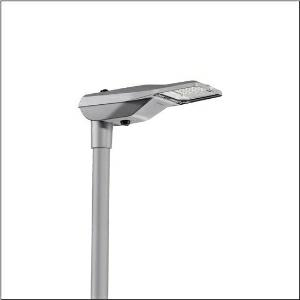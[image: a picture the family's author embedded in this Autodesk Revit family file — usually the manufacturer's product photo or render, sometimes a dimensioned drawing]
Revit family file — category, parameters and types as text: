
# Revit family: streetlight_sl_21_micro___st1_0a_5xe1d43t08db_894b
name_source: partatom
category: Lighting Fixtures
units: mm (PartAtom-declared; Revit-internal decimal feet)

## family parameters
Cut with Voids When Loaded = No
Host = Face
Light Source = No
Part Type = Normal
Room Calculation Point = No
Round Connector Dimension = Use Diameter
Shared = No

## types (1)
- --- (1 x LED, 5320 lm, 39.1 W, 4000K)
    Apparent Load = 39 VA
    CIE Flux Codes = 37 72 97 100 100
    Color Rendering = 70
    Color Temperature = 4000K
    Default Elevation = 1800 mm
    Description = Streetlight SL 21 micro, mast luminaire, primary light control with lens, of PMMA, primary optical cover: cover, of toughened safety glass, transparent, light distribution: ST1.0a, light emission: direct distribution, primary light characteristic: asymmetric, installation type: side-entry, post-top, LED, High Power LED, rated luminous flux: 5.320lm, luminous efficacy: 136lm/W, light colour: 740, colour temperature: 4000K, control gear: D4i, control: flexible luminous flux parameterisation, time-dependent luminous flux control, constant luminous flux control, overheat protection, pre-setting: logarithmic dimming characteristic, mains connection: 220..240V, AC, 50/60Hz, start of lifetime: 39W, end of service life: 41W, reduction: 18W, luminaire housing, of diecast aluminium, powder-coated, SITECO metallic grey (DB 702S), corrosivity category C5 high according to DIN EN ISO 12944, please order mast flange separately, inclination adjustable: 0°, 5°, 10°, 15°, sealing non-destructively replaceable, multi-level sealing system, length: 528mm, width: 235mm, height: 110mm, mast flange for spigot size: 42mm (side-entry): 5XC10008XM4, 60/48mm (side-entry/post-top): 5XC10108XM2, 76/60mm (side-entry/post-top): 5XC10108XM1, Smart Interface below and above, protection rating (complete): IP66, insulation class (complete): insulation class II (safety insulation), certification: CE, ENEC, ENEC+, VDE, impact resistance: IK10, permissible operating ambient temperature for outdoor applications: -40..+50°C, standard-compliant lighting for roads and squares, packaging unit: 1 piece

Light Distribution: ST1.0a
    Height = 110 mm
    Lamp = 1 x LED
    Lamp Light Flux = 5320 lm
    Lamp Power = 39.1 W
    Lamp count = 1
    Length = 528 mm
    Luminous efficacy = 136 lm/W
    Manufacturer = Siteco
    ModVariant = No
    Model = 5XE1D43T08DB
    Number of Poles = 1
    OnlyDefault = Yes
    Power Factor = 1
    Product Name = Streetlight SL 21 micro | ST1.0a
    Product group = mast luminaire | pylon top
    ProductGroupID = 6100
    Protection Class = Protection class II
    Protection Degree = IP 66
    RLX_Detail_Level = 1
    RLX_Emergency_Light_Flux = 0 lm
    RLX_Emergency_Type = 0
    RLX_Emergency_Type_DB = No
    RlxData = <blob elided: 98781 chars, md5=bdcd3f6a>
    Socket = socket
    Standby Power = 0 W
    System Light Flux = 5320 lm
    System Power = 39 W
    Type Comments = factory setting: luminous flux: 100 % | dim-lin: 254 | 765 mA
    Type Image = l_1007239.jpg
    URL = http://relux.com
    VarID = @adj_155213
    Voltage = 0 V
    Weight = 0.00 kg
    Width = 235 mm

## geometry (parser evidence)
native form markers: Blend x4, Sweep x11
no freeform markers — native parametric forms only
